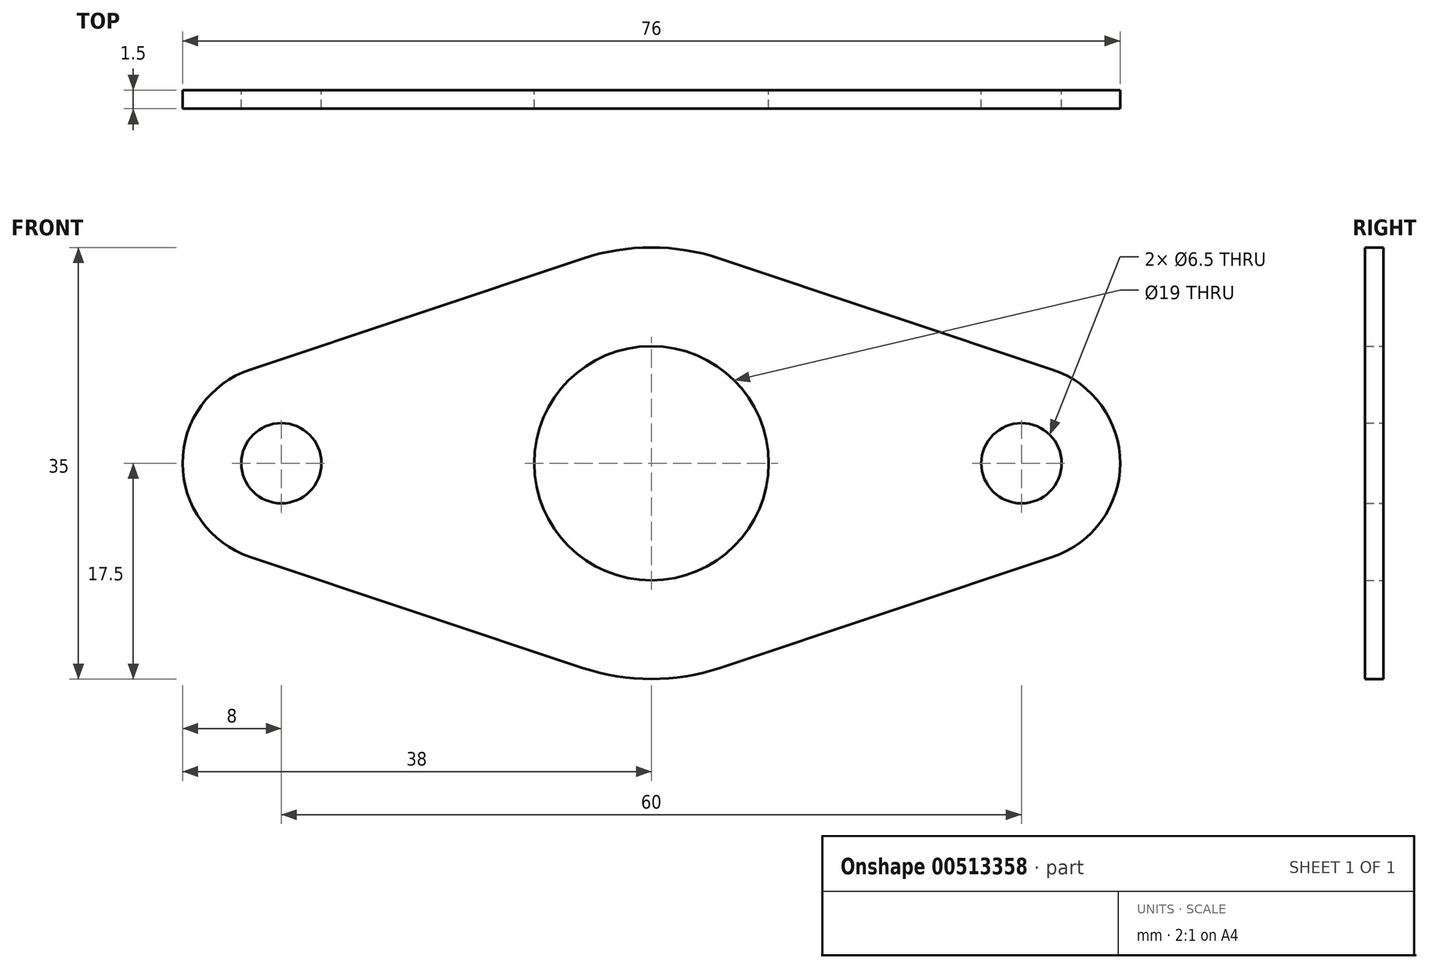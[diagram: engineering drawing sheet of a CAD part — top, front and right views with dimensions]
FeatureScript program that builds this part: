
annotation { "Feature Type Name" : "Feature", "Feature Type Description" : "" }
export const myFeature = defineFeature(function(context is Context, id is Id, definition is map)
    precondition{}
    {
        {
            var Q0;
            Q0=qCreatedBy(makeId("Front.planeOp"),FACE);
            var sketch = newSketch(context, id + "F0", { "sketchPlane" : qUnion([Q0])});
            skLineSegment(sketch, "E0", {"start": v(-44.87, 0) * mm, "end": v(48.3, 0) * mm, "construction": true});
            skLineSegment(sketch, "E1", {"start": v(0, 18.54) * mm, "end": v(0, -22.2) * mm, "construction": true});
            skLineSegment(sketch, "E2", {"start": v(-30, 12.36) * mm, "end": v(-30, -13.5) * mm, "construction": true});
            skLineSegment(sketch, "E3", {"start": v(30, 9.16) * mm, "end": v(30, -10.07) * mm, "construction": true});
            skArc(sketch, "E4", {"start": v(-5.54, -16.6) * mm, "mid": v(0, -17.5) * mm, "end": v(5.54, -16.6) * mm});
            skCircle(sketch, "E5", {"center": v(-30, 0) * mm, "radius": 3.25 * mm});
            skCircle(sketch, "E6", {"center": v(30, 0) * mm, "radius": 3.25 * mm});
            skArc(sketch, "E7", {"start": v(-32.53, 7.59) * mm, "mid": v(-38, 0) * mm, "end": v(-32.53, -7.59) * mm});
            skArc(sketch, "E8", {"start": v(32.53, -7.59) * mm, "mid": v(38, 0) * mm, "end": v(32.53, 7.59) * mm});
            skLineSegment(sketch, "E9", {"start": v(-32.53, 7.59) * mm, "end": v(-5.54, 16.6) * mm});
            skLineSegment(sketch, "E10", {"start": v(5.54, 16.6) * mm, "end": v(32.53, 7.59) * mm});
            skLineSegment(sketch, "E11", {"start": v(-32.53, -7.59) * mm, "end": v(-5.54, -16.6) * mm});
            skLineSegment(sketch, "E12", {"start": v(5.54, -16.6) * mm, "end": v(32.53, -7.59) * mm});
            skArc(sketch, "E13.trimOffspring", {"start": v(5.54, 16.6) * mm, "mid": v(0, 17.5) * mm, "end": v(-5.54, 16.6) * mm});
            skCircle(sketch, "E14", {"center": v(0, 0) * mm, "radius": 9.5 * mm});
            skSolve(sketch);
        }
        {
            var Q0;
            Q0 = qSketchRegion(id + "F0", true);
            extrude(context, id + "F1", {"entities" : qUnion([Q0]), "depth" : 1.5 * mm});
        }
    });
